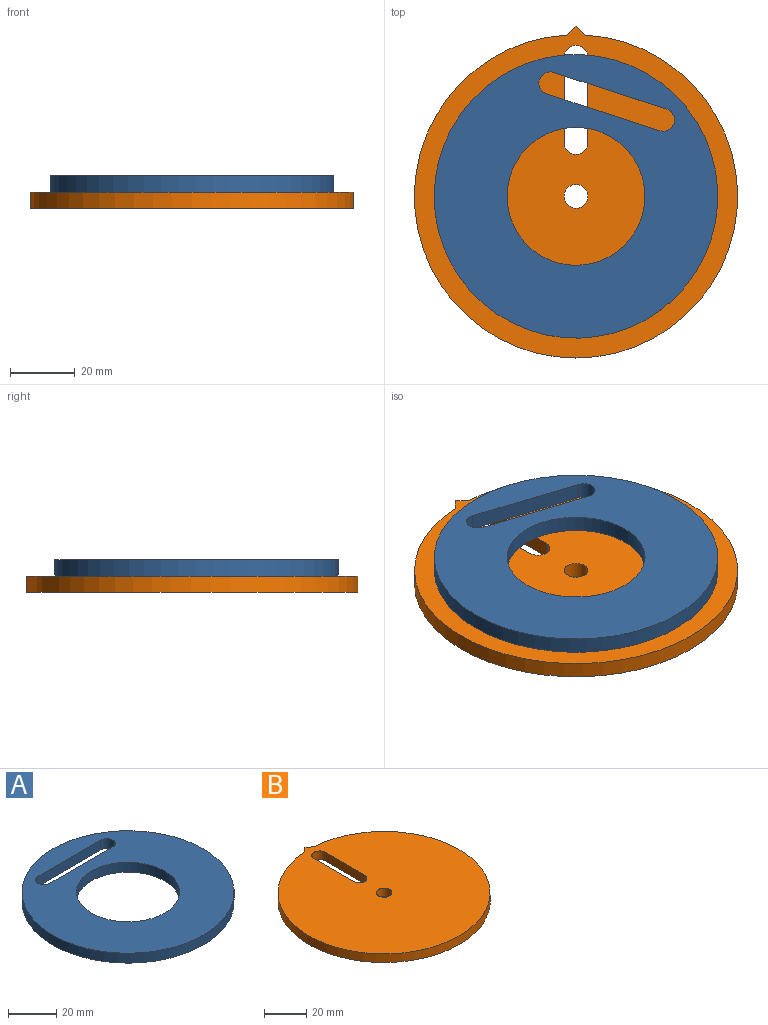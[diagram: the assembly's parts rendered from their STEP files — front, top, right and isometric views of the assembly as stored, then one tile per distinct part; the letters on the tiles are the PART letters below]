
ASSEMBLY  parts=2 mates=1
PART A: 8 faces, bbox 87.7x87.7x5 mm
  f0: cylinder r=3.5mm len=7mm, axis (0,0,-1), area 55mm2, adj f1,f4,f6,f7
  f1: plane 36.75x5mm, normal (0,-1,0), area 183.7mm2, adj f0,f2,f6,f7
  f2: cylinder r=3.5mm len=7mm, axis (0,0,-1), area 55mm2, adj f1,f4,f6,f7
  f3: cylinder r=43.87mm len=87.75mm, axis (0,0,-1), area 1378.3mm2, adj f6,f7
  f4: plane 36.75x5mm, normal (0,1,0), area 183.7mm2, adj f0,f2,f6,f7
  f5: cylinder r=21.33mm len=42.67mm, axis (0,0,-1), area 670.2mm2, adj f6,f7
  f6: plane 87.75x87.75mm, normal (0,0,1), area 4321.8mm2, adj f0,f1,f2,f3,f4,f5
  f7: plane 87.75x87.75mm, normal (0,0,-1), area 4321.8mm2, adj f0,f1,f2,f3,f4,f5
PART B: 10 faces, bbox 100x102.7x5 mm
  f0: cylinder r=50mm len=100mm, axis (0,0,-1), area 1541.8mm2, adj f1,f7,f8,f9
  f1: plane 5x2.89mm, normal (0.69,0.72,0), area 20.1mm2, adj f0,f7,f8,f9
  f2: plane 26.36x5mm, normal (1,0,0), area 131.8mm2, adj f3,f6,f8,f9
  f3: cylinder r=3.69mm len=7.37mm, axis (0,0,-1), area 57.9mm2, adj f2,f4,f8,f9
  f4: plane 26.36x5mm, normal (-1,0,0), area 131.8mm2, adj f3,f6,f8,f9
  f5: cylinder r=3.69mm len=7.37mm, axis (0,0,-1), area 115.8mm2, adj f8,f9
  f6: cylinder r=3.69mm len=7.37mm, axis (0,0,-1), area 57.9mm2, adj f2,f4,f8,f9
  f7: plane 5x2.89mm, normal (-0.69,0.72,0), area 20.1mm2, adj f0,f1,f8,f9
  f8: plane 102.71x100mm, normal (0,0,1), area 7581.9mm2, adj f0,f1,f2,f3,f4,f5,f6,f7
  f9: plane 102.71x100mm, normal (0,0,-1), area 7581.9mm2, adj f0,f1,f2,f3,f4,f5,f6,f7
PLACE A rot(axis=(0,0,-1),18deg) t=(0,0,0)mm
PLACE B at identity fixed
MATE revolute B.f5 <-> A.f5  axis (0,0,1) through (0,0,5)mm
